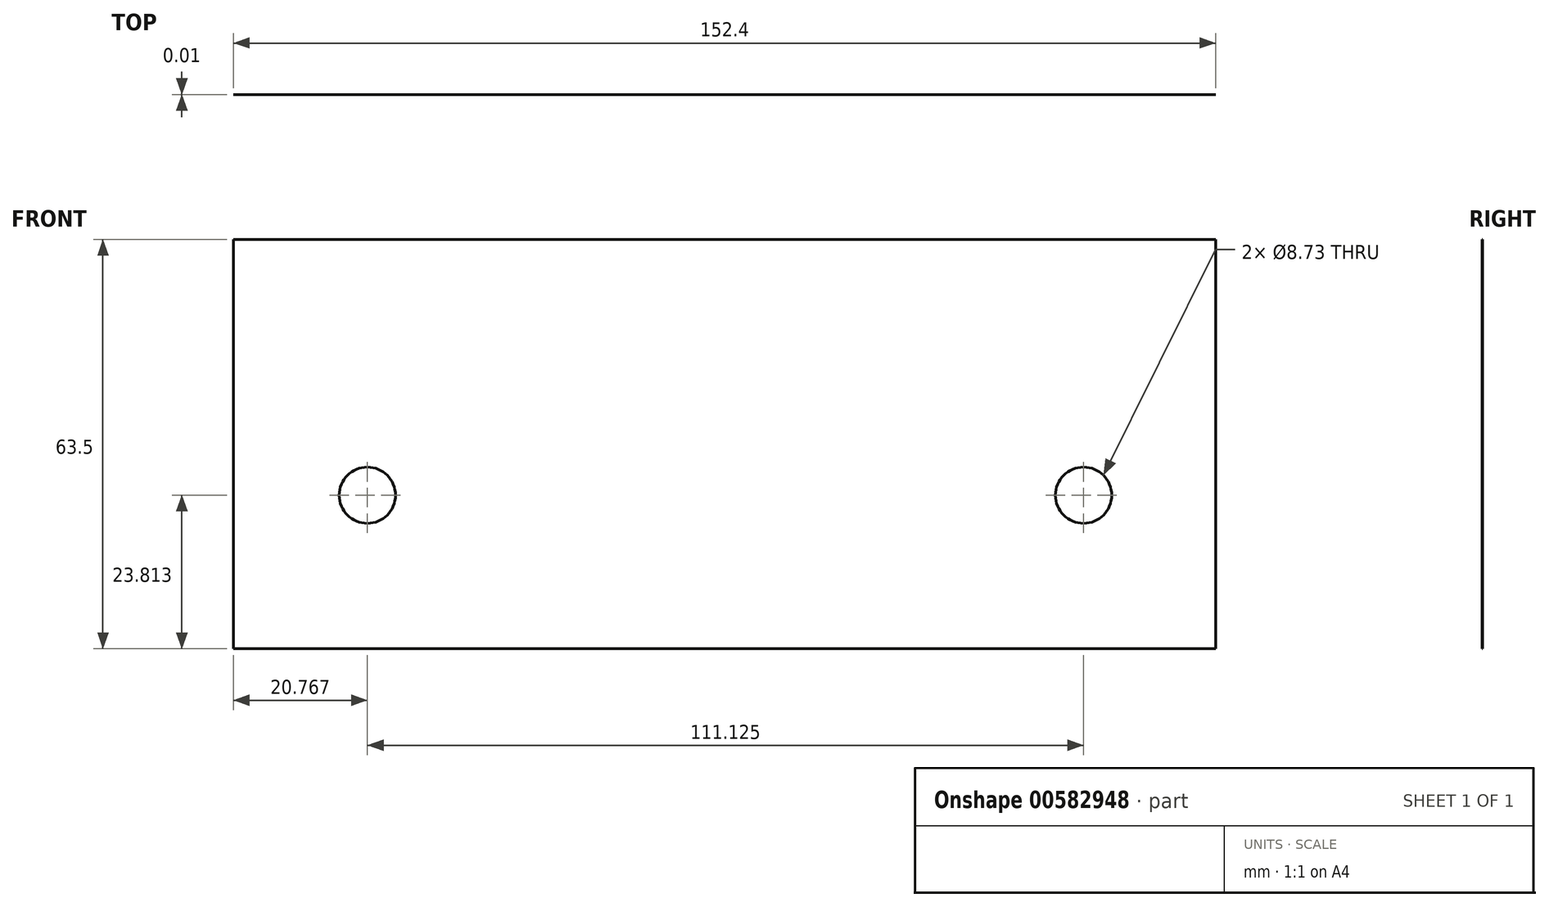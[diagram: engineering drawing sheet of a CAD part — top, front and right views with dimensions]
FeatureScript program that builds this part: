
annotation { "Feature Type Name" : "Feature", "Feature Type Description" : "" }
export const myFeature = defineFeature(function(context is Context, id is Id, definition is map)
    precondition{}
    {
        {
            var Q0;
            Q0=qCreatedBy(makeId("Front.planeOp"),FACE);
            var sketch = newSketch(context, id + "F0", { "sketchPlane" : qUnion([Q0])});
            skLineSegment(sketch, "E0.bottom", {"start": v(-78.99, 4.73) * mm, "end": v(73.41, 4.73) * mm});
            skLineSegment(sketch, "E0.top", {"start": v(-78.99, -58.77) * mm, "end": v(73.41, -58.77) * mm});
            skLineSegment(sketch, "E0.left", {"start": v(-78.99, 4.73) * mm, "end": v(-78.99, -58.77) * mm});
            skLineSegment(sketch, "E0.right", {"start": v(73.41, 4.73) * mm, "end": v(73.41, -58.77) * mm});
            skSolve(sketch);
        }
        {
            var Q0;
            Q0=makeQuery(id+"F0.imprint","IMPRINT",FACE,{"disambiguationData":[TD([[makeQuery(id+"F0.imprint","IMPRINT",EDGE,{"derivedFrom":sQuery(id+"F0.wireOp",EDGE,"E0.bottom")}),-1.0]])]});
            extrude(context, id + "F1", {"entities" : qUnion([Q0]), "depth" : 3 / 203.2 * mm, "offsetDistance" : 25.4 * mm});
        }
        {
            var Q0;
            Q0=makeQuery(id+"F1.opExtrude","CAP_FACE",FACE,{"disambiguationData":[OSD([sQuery(id+"F0.wireOp",EDGE,"E0.bottom"),sQuery(id+"F0.wireOp",EDGE,"E0.top"),sQuery(id+"F0.wireOp",EDGE,"E0.left"),sQuery(id+"F0.wireOp",EDGE,"E0.right")])],"isStart":false});
            var sketch = newSketch(context, id + "F2", { "sketchPlane" : qUnion([Q0])});
            skCircle(sketch, "E1", {"center": v(-58.22, -34.96) * mm, "radius": 4.37 * mm});
            skCircle(sketch, "E2", {"center": v(52.9, -34.96) * mm, "radius": 4.37 * mm});
            skSolve(sketch);
        }
        {
            var Q0;
            Q0=makeQuery(id+"F2.imprint","IMPRINT",FACE,{"disambiguationData":[TD([[makeQuery(id+"F2.imprint","IMPRINT",EDGE,{"derivedFrom":sQuery(id+"F2.wireOp",EDGE,"E2")}),1.0]])]});
            var Q1;
            Q1=makeQuery(id+"F2.imprint","IMPRINT",FACE,{"disambiguationData":[TD([[makeQuery(id+"F2.imprint","IMPRINT",EDGE,{"derivedFrom":sQuery(id+"F2.wireOp",EDGE,"E1")}),1.0]])]});
            extrude(context, id + "F3", {"entities" : qUnion([Q0, Q1]), "operationType" : NewBodyOperationType.REMOVE, "oppositeDirection" : true, "depth" : 25.4 * mm, "offsetDistance" : 25.4 * mm});
        }
        {
            var Q0;
            Q0=sQuery(id+"F2.wireOp",VERTEX,"E2.center");
            var Q1;
            Q1=sQuery(id+"F2.wireOp",VERTEX,"E1.center");
            var Q2;
            Q2=makeQuery(id+"F1.opExtrude","SWEPT_BODY",BODY,{"disambiguationData":[OSD([sQuery(id+"F0.wireOp",EDGE,"E0.bottom"),sQuery(id+"F0.wireOp",EDGE,"E0.top"),sQuery(id+"F0.wireOp",EDGE,"E0.left"),sQuery(id+"F0.wireOp",EDGE,"E0.right")])]});
            hole(context, id + "F4", {"style" : HoleStyle.C_SINK, "endStyle" : HoleEndStyle.THROUGH, "holeDiameter" : 11 / 812.8 * mm, "cSinkDiameter" : 21 / 812.8 * mm, "cSinkAngle" : 90 * degree, "majorDiameter" : 6.35 * mm, "isTappedThrough" : true, "tappedDepth" : 12.7 * mm, "tapClearance" : 3, "startFromSketch" : true, "locations" : qUnion([Q0, Q1]), "scope" : qUnion([Q2])});
        }
    });
